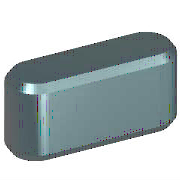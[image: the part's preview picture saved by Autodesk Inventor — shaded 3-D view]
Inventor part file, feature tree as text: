
AUTODESK INVENTOR PART (.ipt)
format: ipt  version: 2025 (Build 290162000, 162)  size: 138,752 bytes
history: native  units: mm (DEFAULTED — no unit token found)
features: plane x3, extrude x1
ambient origin geometry x8: Origin, YZ Plane, XZ Plane, XY Plane, X Axis, Y Axis, Z Axis, Center Point
bodies: Solid1 (feature_tree)
feature tree (4):
  plane  "Work Plane1"
  plane  "Work Plane2"
  extrude  "轴承体1"  Depth=3.0mm
  plane  "Work Plane3"
